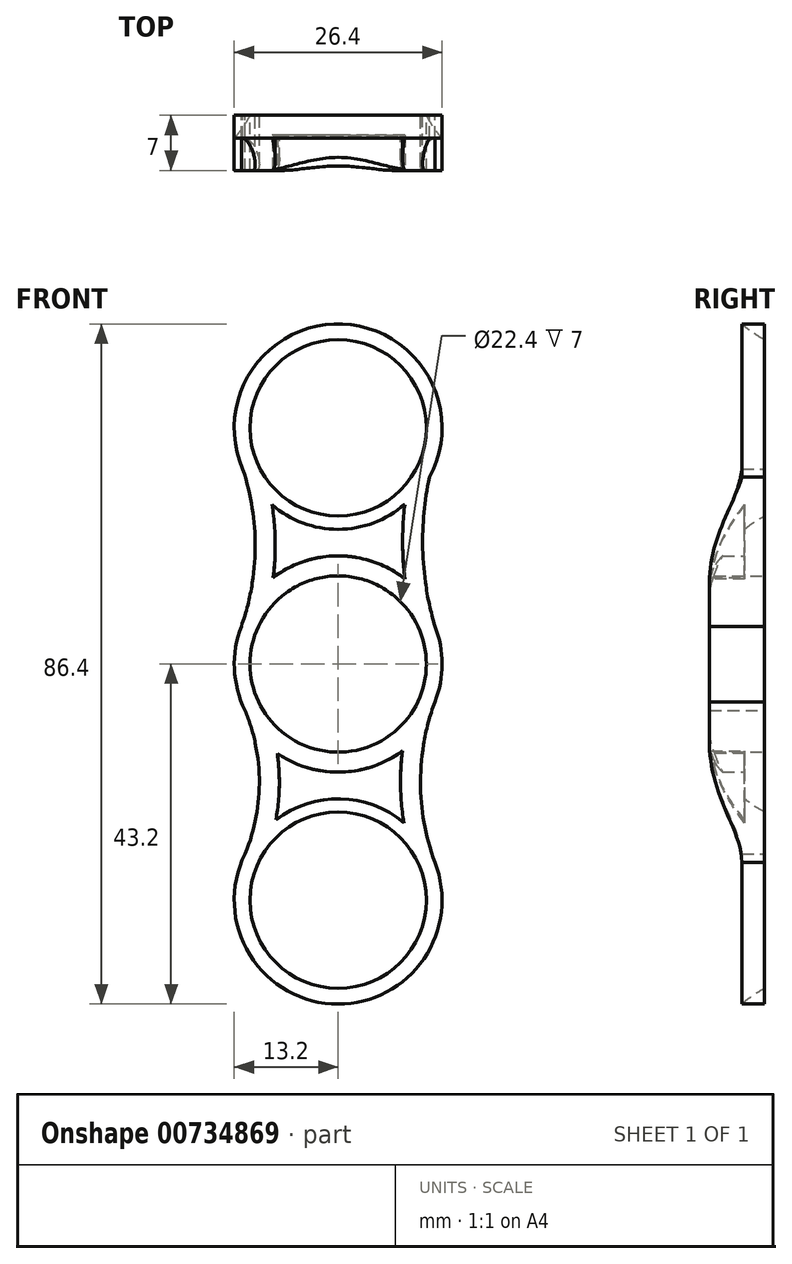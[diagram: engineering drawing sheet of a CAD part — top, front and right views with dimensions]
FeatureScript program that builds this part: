
annotation { "Feature Type Name" : "Feature", "Feature Type Description" : "" }
export const myFeature = defineFeature(function(context is Context, id is Id, definition is map)
    precondition{}
    {
        {
            var Q0;
            Q0=qCreatedBy(makeId("Front.planeOp"),FACE);
            var sketch = newSketch(context, id + "F0", { "sketchPlane" : qUnion([Q0])});
            skCircle(sketch, "E0", {"center": v(0, 0) * mm, "radius": 11.2 * mm});
            skCircle(sketch, "E1", {"center": v(0, 0) * mm, "radius": 13.2 * mm});
            skLineSegment(sketch, "E2", {"start": v(0, 0) * mm, "end": v(0, 30) * mm});
            skCircle(sketch, "E3", {"center": v(0, 30) * mm, "radius": 11.2 * mm});
            skCircle(sketch, "E4", {"center": v(0, 30) * mm, "radius": 13.2 * mm});
            skLineSegment(sketch, "E5", {"start": v(0, 0) * mm, "end": v(0, -30) * mm});
            skCircle(sketch, "E6", {"center": v(0, -30) * mm, "radius": 11.2 * mm});
            skCircle(sketch, "E7", {"center": v(0, -30) * mm, "radius": 13.2 * mm});
            skArc(sketch, "E8", {"start": v(-12.3, 4.8) * mm, "mid": v(-10.6, 17.03) * mm, "end": v(-13.87, 28.94) * mm});
            skArc(sketch, "E9", {"start": v(13.16, 28.94) * mm, "mid": v(10.75, 16.94) * mm, "end": v(12.3, 4.8) * mm});
            skArc(sketch, "E10", {"start": v(-12.3, -25.2) * mm, "mid": v(-10.01, -15) * mm, "end": v(-12.3, -4.8) * mm});
            skArc(sketch, "E11", {"start": v(12.3, -4.8) * mm, "mid": v(10.46, -15) * mm, "end": v(12.3, -25.2) * mm});
            skSolve(sketch);
        }
        {
            var Q0;
            Q0 = qSketchRegion(id + "F0", true);
            extrude(context, id + "F1", {"entities" : qUnion([Q0]), "depth" : 7 * mm, "offsetDistance" : 25.4 * mm});
        }
        {
            var Q0;
            Q0=makeQuery(id+"F1.opExtrude","CAP_EDGE",EDGE,{"disambiguationData":[OSD([sQuery(id+"F0.wireOp",EDGE,"E3")])],"isStart":false});
            fillet(context, id + "F2", {"entities" : qUnion([Q0]), "radius" : 12.7 * mm, "tangentPropagation" : true, "allowEdgeOverflow" : false});
        }
        {
            var Q0;
            Q0=makeQuery(id+"F1.opExtrude","CAP_EDGE",EDGE,{"disambiguationData":[OSD([sQuery(id+"F0.wireOp",EDGE,"E6")])],"isStart":false});
            fillet(context, id + "F3", {"entities" : qUnion([Q0]), "radius" : 12.7 * mm, "tangentPropagation" : true, "allowEdgeOverflow" : false});
        }
        {
            var Q0;
            Q0=makeQuery(id+"F2.opFillet","BLEND_FACE",FACE,{"disambiguationData":[OSD([sQuery(id+"F0.wireOp",EDGE,"E3")])]});
            var Q1;
            Q1=makeQuery(id+"F3.opFillet","BLEND_FACE",FACE,{"disambiguationData":[OSD([sQuery(id+"F0.wireOp",EDGE,"E6")])]});
            shell(context, id + "F4", {"entities" : qUnion([Q0, Q1]), "thickness" : 2.54 * mm});
        }
    });
